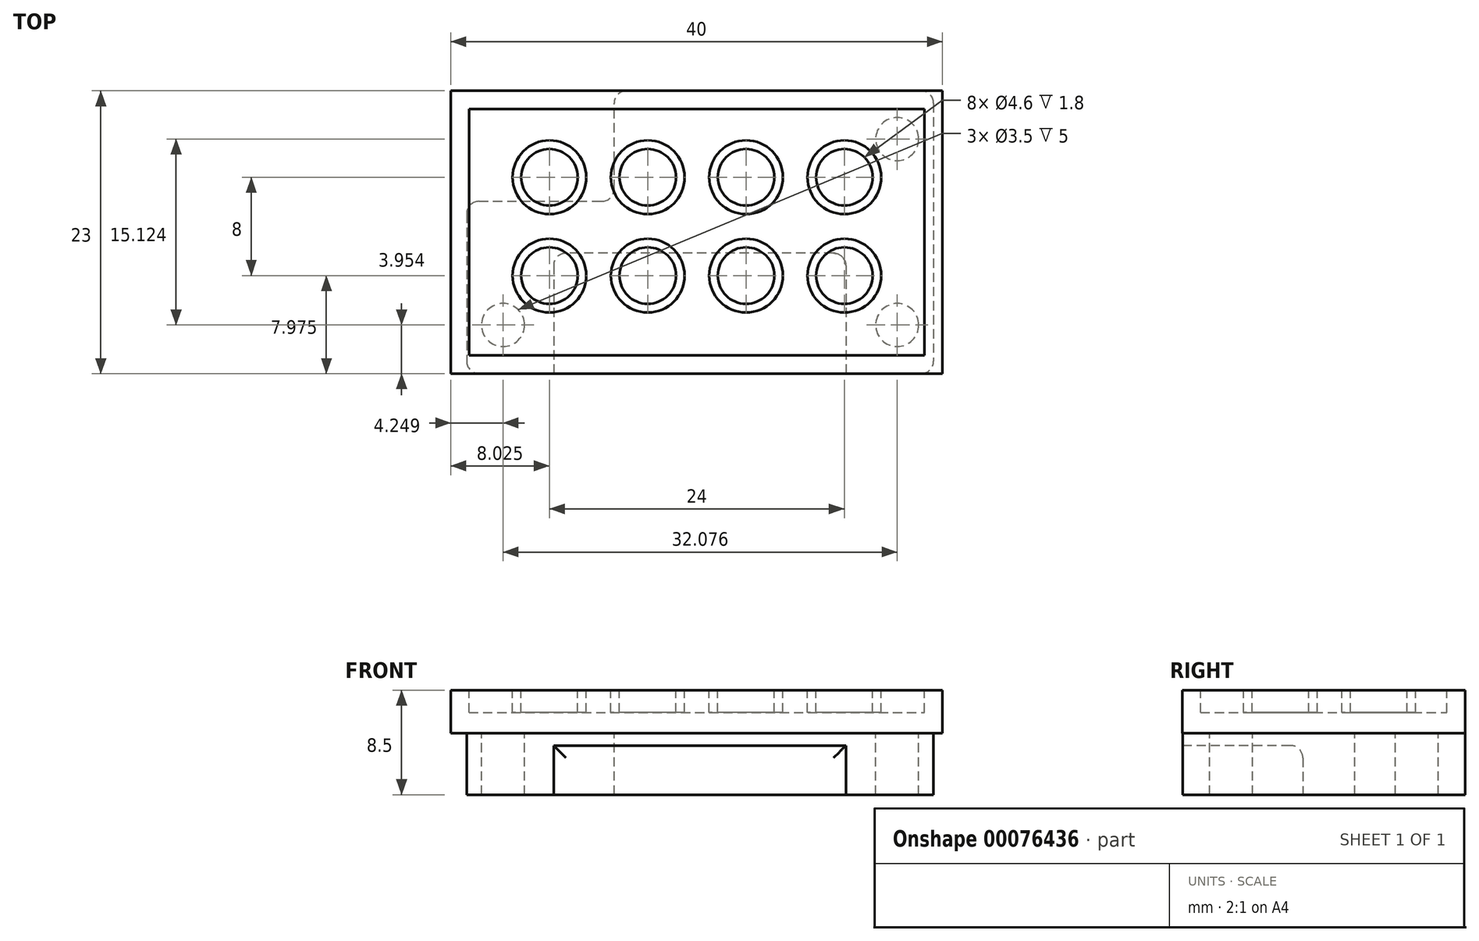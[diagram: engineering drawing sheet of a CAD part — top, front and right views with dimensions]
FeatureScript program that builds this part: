
annotation { "Feature Type Name" : "Feature", "Feature Type Description" : "" }
export const myFeature = defineFeature(function(context is Context, id is Id, definition is map)
    precondition{}
    {
        {
            var Q0;
            Q0=qCreatedBy(makeId("Top.planeOp"),FACE);
            var sketch = newSketch(context, id + "F0", { "sketchPlane" : qUnion([Q0])});
            skLineSegment(sketch, "E0.bottom", {"start": v(0, 0) * mm, "end": v(-40, 0) * mm});
            skLineSegment(sketch, "E0.top", {"start": v(0, 23) * mm, "end": v(-40, 23) * mm});
            skLineSegment(sketch, "E0.left", {"start": v(0, 0) * mm, "end": v(0, 23) * mm});
            skLineSegment(sketch, "E0.right", {"start": v(-40, 0) * mm, "end": v(-40, 23) * mm});
            skSolve(sketch);
        }
        {
            var Q0;
            Q0=makeQuery(id+"F0.imprint","IMPRINT",FACE,{"disambiguationData":[TD([[makeQuery(id+"F0.imprint","IMPRINT",EDGE,{"derivedFrom":sQuery(id+"F0.wireOp",EDGE,"E0.bottom")}),-1.0]])]});
            extrude(context, id + "F1", {"entities" : qUnion([Q0]), "oppositeDirection" : true, "depth" : 3.5 * mm});
        }
        {
            var Q0;
            Q0=qCreatedBy(makeId("Top.planeOp"),FACE);
            var sketch = newSketch(context, id + "F2", { "sketchPlane" : qUnion([Q0])});
            skLineSegment(sketch, "E1.bottom", {"start": v(-38.52, 1.48) * mm, "end": v(-1.47, 1.48) * mm});
            skLineSegment(sketch, "E1.top", {"start": v(-38.52, 21.52) * mm, "end": v(-1.47, 21.53) * mm});
            skLineSegment(sketch, "E1.left", {"start": v(-38.52, 1.48) * mm, "end": v(-38.52, 21.52) * mm});
            skLineSegment(sketch, "E1.right", {"start": v(-1.47, 1.48) * mm, "end": v(-1.47, 21.53) * mm});
            skCircle(sketch, "E2", {"center": v(-7.97, 7.98) * mm, "radius": 3 * mm});
            skCircle(sketch, "E3.0.1.0", {"center": v(-7.97, 15.98) * mm, "radius": 3 * mm});
            skCircle(sketch, "E3.1.0.0", {"center": v(-15.97, 7.98) * mm, "radius": 3 * mm});
            skCircle(sketch, "E3.1.1.0", {"center": v(-15.97, 15.98) * mm, "radius": 3 * mm});
            skCircle(sketch, "E3.2.0.0", {"center": v(-23.97, 7.98) * mm, "radius": 3 * mm});
            skCircle(sketch, "E3.2.1.0", {"center": v(-23.97, 15.98) * mm, "radius": 3 * mm});
            skCircle(sketch, "E3.3.0.0", {"center": v(-31.97, 7.98) * mm, "radius": 3 * mm});
            skCircle(sketch, "E3.3.1.0", {"center": v(-31.97, 15.98) * mm, "radius": 3 * mm});
            skLineSegment(sketch, "E3.direction1", {"start": v(-7.97, 7.98) * mm, "end": v(-15.97, 7.98) * mm, "construction": true});
            skLineSegment(sketch, "E3.direction2", {"start": v(-7.97, 7.98) * mm, "end": v(-7.97, 15.98) * mm, "construction": true});
            skSolve(sketch);
        }
        {
            var Q0;
            {var subQ0=sQuery(id+"F0.wireOp",EDGE,"E0.bottom");var subQ1=sQuery(id+"F0.wireOp",EDGE,"E0.top");var subQ2=sQuery(id+"F0.wireOp",EDGE,"E0.left");var subQ3=sQuery(id+"F0.wireOp",EDGE,"E0.right");Q0=makeQuery(id+"F4.boolean.opBoolean","SPLIT",FACE,{"disambiguationData":[TD([makeQuery(id+"F1.opExtrude","SWEPT_FACE",FACE,{"disambiguationData":[OSD([subQ0])]})])],"derivedFrom":makeQuery(id+"F1.opExtrude","CAP_FACE",FACE,{"disambiguationData":[OSD([subQ0,subQ1,subQ2,subQ3])],"isStart":true})});}
            var sketch = newSketch(context, id + "F3", { "sketchPlane" : qUnion([Q0])});
            skCircle(sketch, "E4", {"center": v(-7.98, 7.97) * mm, "radius": 2.3 * mm});
            skCircle(sketch, "E5.0.1.0", {"center": v(-7.98, 15.97) * mm, "radius": 2.3 * mm});
            skCircle(sketch, "E5.1.0.0", {"center": v(-15.98, 7.97) * mm, "radius": 2.3 * mm});
            skCircle(sketch, "E5.1.1.0", {"center": v(-15.98, 15.97) * mm, "radius": 2.3 * mm});
            skCircle(sketch, "E5.2.0.0", {"center": v(-23.98, 7.97) * mm, "radius": 2.3 * mm});
            skCircle(sketch, "E5.2.1.0", {"center": v(-23.98, 15.97) * mm, "radius": 2.3 * mm});
            skCircle(sketch, "E5.3.0.0", {"center": v(-31.98, 7.97) * mm, "radius": 2.3 * mm});
            skCircle(sketch, "E5.3.1.0", {"center": v(-31.98, 15.97) * mm, "radius": 2.3 * mm});
            skLineSegment(sketch, "E5.direction1", {"start": v(-7.98, 7.97) * mm, "end": v(-15.98, 7.97) * mm, "construction": true});
            skLineSegment(sketch, "E5.direction2", {"start": v(-7.98, 7.97) * mm, "end": v(-7.98, 15.97) * mm, "construction": true});
            skSolve(sketch);
        }
        {
            var Q0;
            Q0=qSketchRegion(id+"F2",true);
            var Q1;
            Q1=qSketchRegion(id+"F3",true);
            var Q2;
            Q2=sQuery(id+"F2.wireOp",EDGE,"de4b574f-d5fe-483e-a269-1c24a673af37.0.MirrorC");
            extrude(context, id + "F4", {"entities" : qUnion([Q0, Q1]), "operationType" : NewBodyOperationType.REMOVE, "surfaceEntities" : qUnion([Q2]), "oppositeDirection" : true, "depth" : 1.8 * mm});
        }
        {
            var Q0;
            Q0=makeQuery(id+"F1.opExtrude","CAP_FACE",FACE,{"disambiguationData":[OSD([sQuery(id+"F0.wireOp",EDGE,"E0.bottom"),sQuery(id+"F0.wireOp",EDGE,"E0.top"),sQuery(id+"F0.wireOp",EDGE,"E0.left"),sQuery(id+"F0.wireOp",EDGE,"E0.right")])],"isStart":false});
            var sketch = newSketch(context, id + "F5", { "sketchPlane" : qUnion([Q0])});
            skLineSegment(sketch, "E6.bottom", {"start": v(-0.71, -23.02) * mm, "end": v(-26.71, -23.02) * mm});
            skLineSegment(sketch, "E6.top", {"start": v(-0.71, -0.02) * mm, "end": v(-38.71, -0.02) * mm});
            skLineSegment(sketch, "E6.left", {"start": v(-0.71, -23.02) * mm, "end": v(-0.71, -0.02) * mm});
            skLineSegment(sketch, "E6.right", {"start": v(-38.71, -14.02) * mm, "end": v(-38.71, -0.02) * mm});
            skPoint(sketch, "E6.middle", {"position": v(-19.71, -11.52) * mm});
            skCircle(sketch, "E7", {"center": v(-3.68, -3.95) * mm, "radius": 1.75 * mm});
            skCircle(sketch, "E8.MirrorC", {"center": v(-3.68, -19.08) * mm, "radius": 1.75 * mm});
            skCircle(sketch, "E9.MirrorC", {"center": v(-35.75, -3.95) * mm, "radius": 1.75 * mm});
            skLineSegment(sketch, "E10.bottom", {"start": v(-38.71, -14.02) * mm, "end": v(-26.71, -14.02) * mm});
            skLineSegment(sketch, "E10.right", {"start": v(-26.71, -14.02) * mm, "end": v(-26.71, -23.02) * mm});
            skPoint(sketch, "E11.orphan", {"position": v(-38.71, -23.02) * mm});
            skPoint(sketch, "E12.end.orphan", {"position": v(-19.71, -23.02) * mm});
            skPoint(sketch, "E13.end.orphan", {"position": v(-19.71, -0.02) * mm});
            skSolve(sketch);
        }
        {
            var Q0;
            {var subQ1=sQuery(id+"F5.wireOp",EDGE,"E6.top");Q0=makeQuery(id+"F5.imprint","IMPRINT",FACE,{"disambiguationData":[TD([[makeQuery(id+"F5.imprint","IMPRINT",EDGE,{"derivedFrom":subQ1}),1.0]])]});}
            extrude(context, id + "F6", {"entities" : qUnion([Q0]), "operationType" : NewBodyOperationType.ADD, "depth" : 5 * mm});
        }
        {
            var Q0;
            Q0=makeQuery(id+"F6.opExtrude","CAP_FACE",FACE,{"disambiguationData":[OSD([sQuery(id+"F0.wireOp",EDGE,"E0.top"),sQuery(id+"F5.wireOp",EDGE,"E6.top"),sQuery(id+"F5.wireOp",EDGE,"E6.left"),sQuery(id+"F5.wireOp",EDGE,"E6.right"),sQuery(id+"F5.wireOp",EDGE,"E7"),sQuery(id+"F5.wireOp",EDGE,"E8.MirrorC"),sQuery(id+"F5.wireOp",EDGE,"E9.MirrorC"),sQuery(id+"F5.wireOp",EDGE,"E10.bottom"),sQuery(id+"F5.wireOp",EDGE,"E10.right")])],"isStart":false});
            var sketch = newSketch(context, id + "F7", { "sketchPlane" : qUnion([Q0])});
            skLineSegment(sketch, "E14.bottom", {"start": v(-7.86, -9.8) * mm, "end": v(-31.63, -9.8) * mm});
            skLineSegment(sketch, "E14.top", {"start": v(-7.86, -0.02) * mm, "end": v(-31.63, -0.02) * mm});
            skLineSegment(sketch, "E14.left", {"start": v(-7.86, -9.8) * mm, "end": v(-7.86, -0.02) * mm});
            skLineSegment(sketch, "E14.right", {"start": v(-31.63, -9.8) * mm, "end": v(-31.63, -0.02) * mm});
            skSolve(sketch);
        }
        {
            var Q0;
            Q0 = qSketchRegion(id + "F7", true);
            extrude(context, id + "F8", {"entities" : qUnion([Q0]), "operationType" : NewBodyOperationType.REMOVE, "oppositeDirection" : true, "depth" : 4 * mm});
        }
        {
            var Q0;
            Q0=makeQuery(id+"F8.boolean.opBoolean","COPY",EDGE,{"derivedFrom":makeQuery(id+"F8.opExtrude","SWEPT_EDGE",EDGE,{"disambiguationData":[OSD([sQuery(id+"F7.wireOp",EDGE,"E14.bottom"),sQuery(id+"F7.wireOp",EDGE,"E14.right")])]})});
            var Q1;
            Q1=makeQuery(id+"F8.boolean.opBoolean","COPY",EDGE,{"derivedFrom":makeQuery(id+"F8.opExtrude","SWEPT_EDGE",EDGE,{"disambiguationData":[OSD([sQuery(id+"F7.wireOp",EDGE,"E14.bottom"),sQuery(id+"F7.wireOp",EDGE,"E14.left")])]})});
            var Q2;
            Q2=makeQuery(id+"F6.opExtrude","SWEPT_EDGE",EDGE,{"disambiguationData":[OSD([sQuery(id+"F5.wireOp",EDGE,"E10.bottom"),sQuery(id+"F5.wireOp",EDGE,"E10.right")])]});
            var Q3;
            Q3=makeQuery(id+"F8.boolean.opBoolean","COPY",EDGE,{"derivedFrom":makeQuery(id+"F8.opExtrude","CAP_EDGE",EDGE,{"disambiguationData":[OSD([sQuery(id+"F7.wireOp",EDGE,"E14.bottom")])],"isStart":false})});
            var Q4;
            Q4=makeQuery(id+"F6.opExtrude","SWEPT_EDGE",EDGE,{"disambiguationData":[OSD([sQuery(id+"F5.wireOp",EDGE,"E6.top"),sQuery(id+"F5.wireOp",EDGE,"E6.left")])]});
            var Q5;
            Q5=makeQuery(id+"F6.opExtrude","SWEPT_EDGE",EDGE,{"disambiguationData":[OSD([sQuery(id+"F5.wireOp",EDGE,"E6.top"),sQuery(id+"F5.wireOp",EDGE,"E6.right")])]});
            var Q6;
            Q6=makeQuery(id+"F6.opExtrude","SWEPT_EDGE",EDGE,{"disambiguationData":[OSD([sQuery(id+"F5.wireOp",EDGE,"E6.right"),sQuery(id+"F5.wireOp",EDGE,"E10.bottom")])]});
            var Q7;
            Q7=makeQuery(id+"F6.opExtrude","SWEPT_EDGE",EDGE,{"disambiguationData":[OSD([sQuery(id+"F0.wireOp",EDGE,"E0.top"),sQuery(id+"F5.wireOp",EDGE,"E10.right")])]});
            var Q8;
            Q8=makeQuery(id+"F6.opExtrude","SWEPT_EDGE",EDGE,{"disambiguationData":[OSD([sQuery(id+"F0.wireOp",EDGE,"E0.top"),sQuery(id+"F5.wireOp",EDGE,"E6.left")])]});
            fillet(context, id + "F9", {"entities" : qUnion([Q0, Q1, Q2, Q3, Q4, Q5, Q6, Q7, Q8]), "radius" : 1 * mm, "tangentPropagation" : true, "allowEdgeOverflow" : false});
        }
    });
